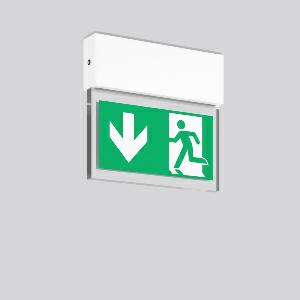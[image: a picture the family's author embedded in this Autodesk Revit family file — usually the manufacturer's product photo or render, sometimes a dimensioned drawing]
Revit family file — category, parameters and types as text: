
# Revit family: halyxx_671742_002_1_07_e627
name_source: partatom
category: Lighting Fixtures
units: mm (PartAtom-declared; Revit-internal decimal feet)

## family parameters
Cut with Voids When Loaded = No
Host = Face
Light Source = No
Part Type = Normal
Room Calculation Point = No
Round Connector Dimension = Use Diameter
Shared = No

## types (1)
- HALYXX (1 x LED Modul 840, 55 lm, 4000)
    Apparent Load = 3 VA
    Approval mark = CE
    CIE Flux Codes = 18 46 76 54 100
    Color Rendering = 80
    Color Temperature = 4000
    Default Elevation = 1800 mm
    Description = Series: HALYXX
Luminaire for escape route identification. Housing: extruded aluminium profile, anodised or powder-coated. Display panel: highly transparent panel, plastic, with legend on one side/both sides. Electronic ballast included. Self-contained system with automatic self-test and feedback via DALI bus, only to RZB DALI monitoring system. Please indicate legend number when placing your order! 
Colour: white
Length: 235 mm
Width: 40 mm
Height: 220 mm
Weight: 1.46 kg
Operating mode: maintained power mode
Viewing Distance: 19 m
Duration time: 3 h
Lamp: LED
Socket: without socket
Colour temperature: 4000K
Colour rendering index (CRI): 80
System power: 3.2 W
Rated luminous flux: 55 lm
Luminous flux, emergency: 30
System power, emergency: -
Control gear: Electronic transformer
Protection class: I
Type of protection: IP 40
    Height = 220 mm
    Lamp = 1 x LED Modul 840
    Lamp Light Flux = 55 lm
    Lamp count = 1
    Length = 235 mm
    Lifetime = 50000 h
    Luminous efficacy = 17 lm/W
    Manufacturer = RZB
    ModVariant = No
    Model = 671742.002.1.07
    Mounting Place = Ceiling
    Mounting Type = Surface mounted
    Number of Poles = 1
    OnlyDefault = Yes
    Power Factor = 1
    Product Name = HALYXX
    Product group = Surface mounted ceiling luminaires
    ProductGroupID = 303
    Protection Class = Protection class I
    Protection Degree = IP 40
    RLX_Detail_Level = 1
    RLX_Emergency_Light_Flux = 30 lm
    RLX_Emergency_Type = 3
    RLX_Emergency_Type_DB = Yes
    RlxData = <blob elided: 40793 chars, md5=7cdb449b>
    Socket = socket
    Standby Power = 0 W
    System Light Flux = 55 lm
    System Power = 3 W
    Type Comments = Product without accessories
    Type Image = 671742.002.jpg
    URL = http://relux.com
    VarID = ---
    Voltage = 230 V
    Voltage Range = 220-240 V
    Weight = 0.00 kg
    Width = 40 mm  [stored 0.131234 ft]

note: [stored X ft] marks values corroborated as IEEE doubles in the binary element streams (Revit-internal decimal feet)

## geometry (parser evidence)
native form markers: Blend x4, Sweep x13
no freeform markers — native parametric forms only
